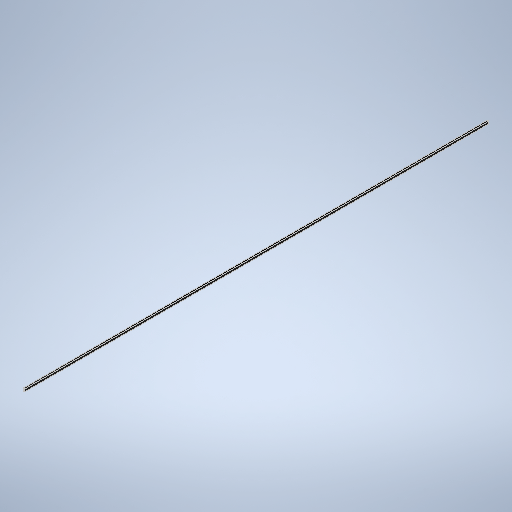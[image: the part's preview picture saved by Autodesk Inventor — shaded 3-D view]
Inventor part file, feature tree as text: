
AUTODESK INVENTOR PART (.ipt)
format: ipt  version: 2025.1 (Build 291241020, 241B)  size: 253,440 bytes
history: native  units: in
note: dims shown in document units (in); Inventor stores cm internally (conversion verified against a paired STEP export)
features: extrude x1, sketch x1
ambient origin geometry x8: Origin, YZ Plane, XZ Plane, XY Plane, X Axis, Y Axis, Z Axis, Center Point
bodies: Solid1 (feature_tree)
feature tree (2):
  extrude  "Extrusion1"  Depth=1.0in
  sketch  "Sketch1"  dims[d0=1.5in d1=1.0in d2=288.0in d3=0.0in]
